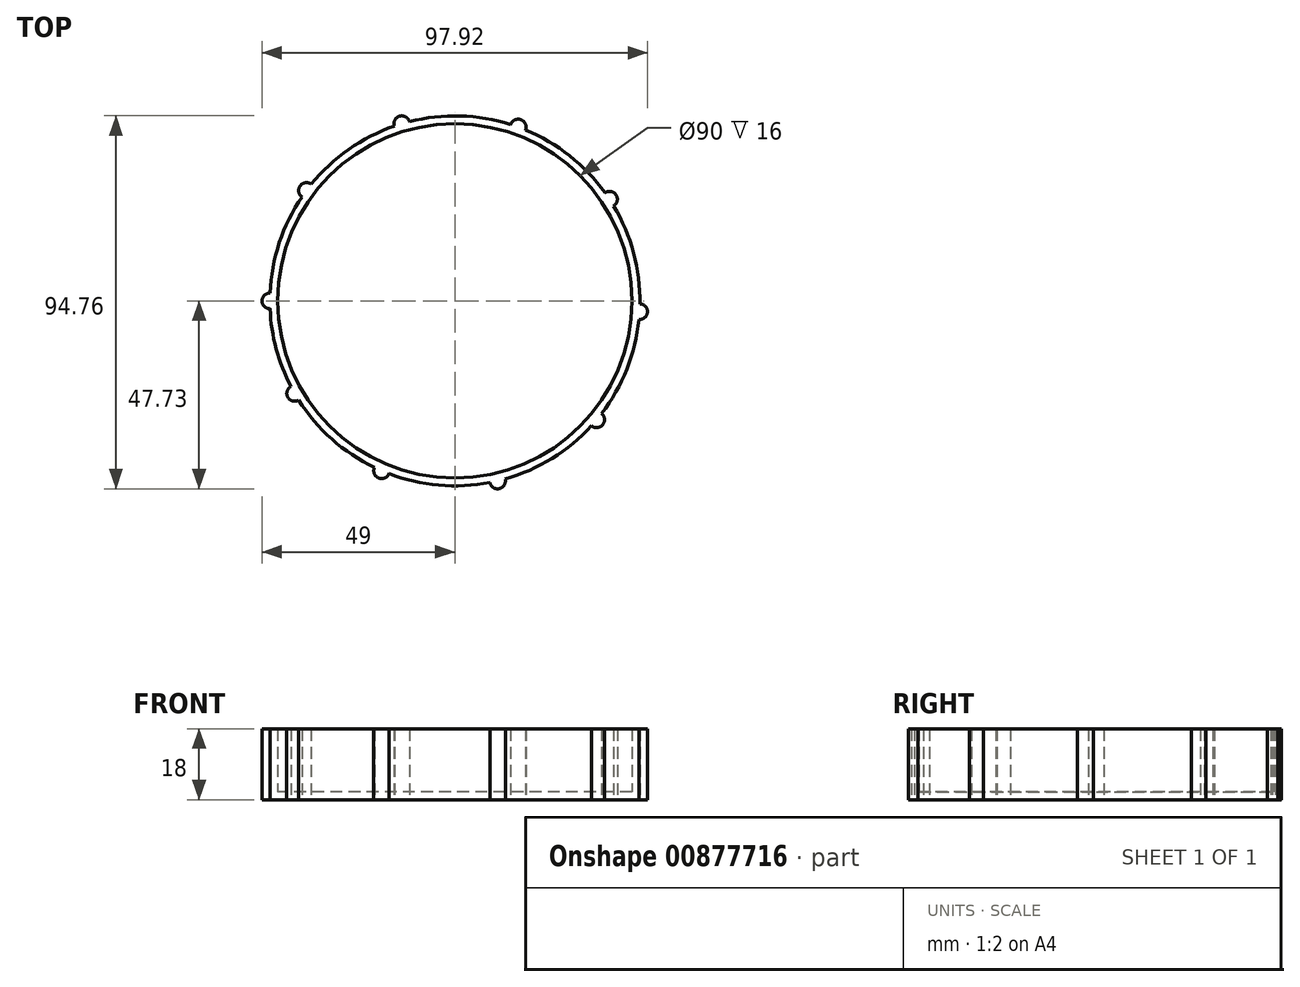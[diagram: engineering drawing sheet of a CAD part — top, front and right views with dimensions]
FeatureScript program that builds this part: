
annotation { "Feature Type Name" : "Feature", "Feature Type Description" : "" }
export const myFeature = defineFeature(function(context is Context, id is Id, definition is map)
    precondition{}
    {
        {
            var Q0;
            Q0=qCreatedBy(makeId("Top.planeOp"),FACE);
            var sketch = newSketch(context, id + "F0", { "sketchPlane" : qUnion([Q0])});
            skCircle(sketch, "E0", {"center": v(0, 0) * mm, "radius": 47 * mm});
            skCircle(sketch, "E1", {"center": v(0, 0) * mm, "radius": 45 * mm});
            skLineSegment(sketch, "E2", {"start": v(0, 0) * mm, "end": v(-47, 0) * mm, "construction": true});
            skLineSegment(sketch, "E3", {"start": v(-47, 0) * mm, "end": v(47, 0) * mm, "construction": true});
            skArc(sketch, "E4", {"start": v(-46.96, 2) * mm, "mid": v(-49, 0) * mm, "end": v(-46.96, -2) * mm});
            skArc(sketch, "E5.1.0", {"start": v(-36.47, 29.64) * mm, "mid": v(-39.3, 29.26) * mm, "end": v(-38.86, 26.44) * mm});
            skArc(sketch, "E5.2.0", {"start": v(-11.55, 45.56) * mm, "mid": v(-14.05, 46.94) * mm, "end": v(-15.38, 44.41) * mm});
            skArc(sketch, "E5.3.0", {"start": v(17.94, 43.44) * mm, "mid": v(16.76, 46.04) * mm, "end": v(14.18, 44.8) * mm});
            skArc(sketch, "E5.4.0", {"start": v(40.33, 24.13) * mm, "mid": v(40.94, 26.93) * mm, "end": v(38.13, 27.47) * mm});
            skArc(sketch, "E5.5.0", {"start": v(46.76, -4.73) * mm, "mid": v(48.92, -2.85) * mm, "end": v(47, -0.73) * mm});
            skArc(sketch, "E5.6.0", {"start": v(34.69, -31.72) * mm, "mid": v(37.54, -31.5) * mm, "end": v(37.26, -28.65) * mm});
            skArc(sketch, "E5.7.0", {"start": v(8.88, -46.15) * mm, "mid": v(11.3, -47.68) * mm, "end": v(12.77, -45.23) * mm});
            skArc(sketch, "E5.8.0", {"start": v(-20.43, -42.33) * mm, "mid": v(-19.4, -45) * mm, "end": v(-16.76, -43.9) * mm});
            skArc(sketch, "E5.9.0", {"start": v(-41.67, -21.75) * mm, "mid": v(-42.44, -24.5) * mm, "end": v(-39.67, -25.21) * mm});
            skLineSegment(sketch, "E5.anchor1", {"start": v(0, 0) * mm, "end": v(-46.96, -2) * mm, "construction": true});
            skLineSegment(sketch, "E5.anchor2", {"start": v(0, 0) * mm, "end": v(-39.67, -25.21) * mm, "construction": true});
            skSolve(sketch);
        }
        {
            var Q0;
            Q0=makeQuery(id+"F0.imprint","IMPRINT",FACE,{"disambiguationData":[TD([[makeQuery(id+"F0.imprint","IMPRINT",EDGE,{"derivedFrom":sQuery(id+"F0.wireOp",EDGE,"E1")}),1.0]])]});
            extrude(context, id + "F1", {"entities" : qUnion([Q0]), "depth" : 2 * mm, "offsetDistance" : 25 * mm});
        }
        {
            var Q0;
            Q0=makeQuery(id+"F0.imprint","IMPRINT",FACE,{"disambiguationData":[TD([[makeQuery(id+"F0.imprint","IMPRINT",EDGE,{"derivedFrom":sQuery(id+"F0.wireOp",EDGE,"E0")}),1.0]])]});
            var Q1;
            {var subQ0=sQuery(id+"F0.wireOp",EDGE,"E4");Q1=makeQuery(id+"F0.imprint","IMPRINT",FACE,{"disambiguationData":[TD([[makeQuery(id+"F0.imprint","IMPRINT",EDGE,{"derivedFrom":subQ0}),1.0]])]});}
            var Q2;
            {var subQ0=sQuery(id+"F0.wireOp",EDGE,"E5.9.0");Q2=makeQuery(id+"F0.imprint","IMPRINT",FACE,{"disambiguationData":[TD([[makeQuery(id+"F0.imprint","IMPRINT",EDGE,{"derivedFrom":subQ0}),1.0]])]});}
            var Q3;
            {var subQ0=sQuery(id+"F0.wireOp",EDGE,"E5.8.0");Q3=makeQuery(id+"F0.imprint","IMPRINT",FACE,{"disambiguationData":[TD([[makeQuery(id+"F0.imprint","IMPRINT",EDGE,{"derivedFrom":subQ0}),1.0]])]});}
            var Q4;
            {var subQ0=sQuery(id+"F0.wireOp",EDGE,"E5.7.0");Q4=makeQuery(id+"F0.imprint","IMPRINT",FACE,{"disambiguationData":[TD([[makeQuery(id+"F0.imprint","IMPRINT",EDGE,{"derivedFrom":subQ0}),1.0]])]});}
            var Q5;
            {var subQ0=sQuery(id+"F0.wireOp",EDGE,"E5.6.0");Q5=makeQuery(id+"F0.imprint","IMPRINT",FACE,{"disambiguationData":[TD([[makeQuery(id+"F0.imprint","IMPRINT",EDGE,{"derivedFrom":subQ0}),1.0]])]});}
            var Q6;
            {var subQ0=sQuery(id+"F0.wireOp",EDGE,"E5.5.0");Q6=makeQuery(id+"F0.imprint","IMPRINT",FACE,{"disambiguationData":[TD([[makeQuery(id+"F0.imprint","IMPRINT",EDGE,{"derivedFrom":subQ0}),1.0]])]});}
            var Q7;
            {var subQ0=sQuery(id+"F0.wireOp",EDGE,"E5.4.0");Q7=makeQuery(id+"F0.imprint","IMPRINT",FACE,{"disambiguationData":[TD([[makeQuery(id+"F0.imprint","IMPRINT",EDGE,{"derivedFrom":subQ0}),1.0]])]});}
            var Q8;
            {var subQ0=sQuery(id+"F0.wireOp",EDGE,"E5.3.0");Q8=makeQuery(id+"F0.imprint","IMPRINT",FACE,{"disambiguationData":[TD([[makeQuery(id+"F0.imprint","IMPRINT",EDGE,{"derivedFrom":subQ0}),1.0]])]});}
            var Q9;
            {var subQ0=sQuery(id+"F0.wireOp",EDGE,"E5.2.0");Q9=makeQuery(id+"F0.imprint","IMPRINT",FACE,{"disambiguationData":[TD([[makeQuery(id+"F0.imprint","IMPRINT",EDGE,{"derivedFrom":subQ0}),1.0]])]});}
            var Q10;
            {var subQ0=sQuery(id+"F0.wireOp",EDGE,"E5.1.0");Q10=makeQuery(id+"F0.imprint","IMPRINT",FACE,{"disambiguationData":[TD([[makeQuery(id+"F0.imprint","IMPRINT",EDGE,{"derivedFrom":subQ0}),1.0]])]});}
            extrude(context, id + "F2", {"entities" : qUnion([Q0, Q1, Q2, Q3, Q4, Q5, Q6, Q7, Q8, Q9, Q10]), "operationType" : NewBodyOperationType.ADD, "depth" : 18 * mm, "offsetDistance" : 25 * mm});
        }
    });
